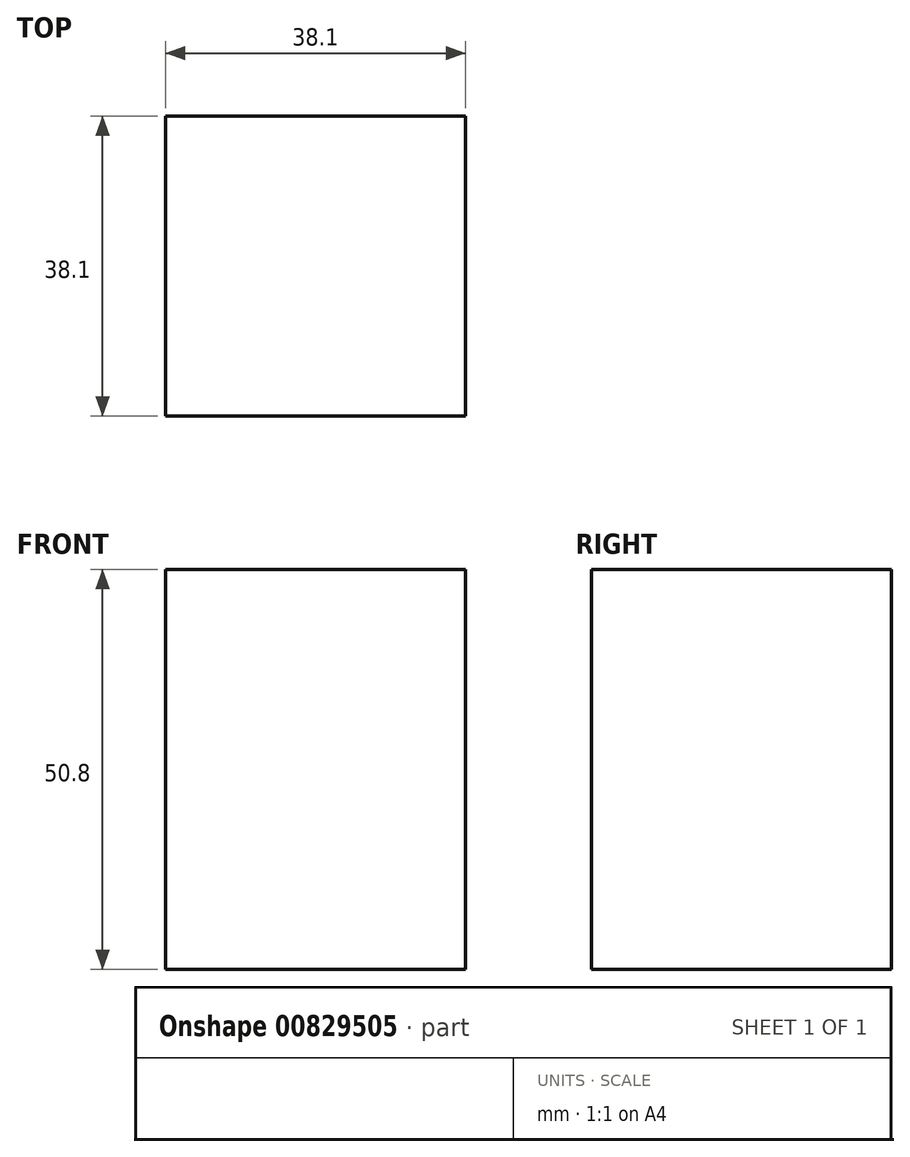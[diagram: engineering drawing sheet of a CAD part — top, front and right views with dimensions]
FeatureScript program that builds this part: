
annotation { "Feature Type Name" : "Feature", "Feature Type Description" : "" }
export const myFeature = defineFeature(function(context is Context, id is Id, definition is map)
    precondition{}
    {
        {
            var Q0;
            Q0=qCreatedBy(makeId("Top.planeOp"),FACE);
            var sketch = newSketch(context, id + "F0", { "sketchPlane" : qUnion([Q0])});
            skLineSegment(sketch, "E0.bottom", {"start": v(0, 0) * mm, "end": v(38.1, 0) * mm});
            skLineSegment(sketch, "E0.top", {"start": v(0, -38.1) * mm, "end": v(38.1, -38.1) * mm});
            skLineSegment(sketch, "E0.left", {"start": v(0, 0) * mm, "end": v(0, -38.1) * mm});
            skLineSegment(sketch, "E0.right", {"start": v(38.1, 0) * mm, "end": v(38.1, -38.1) * mm});
            skSolve(sketch);
        }
        {
            var Q0;
            Q0=makeQuery(id+"F0.imprint","IMPRINT",FACE,{"disambiguationData":[TD([[makeQuery(id+"F0.imprint","IMPRINT",EDGE,{"derivedFrom":sQuery(id+"F0.wireOp",EDGE,"E0.bottom")}),-1.0]])]});
            extrude(context, id + "F1", {"entities" : qUnion([Q0]), "depth" : 50.8 * mm, "offsetDistance" : 25.4 * mm});
        }
    });
